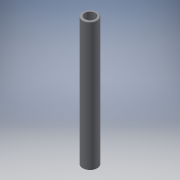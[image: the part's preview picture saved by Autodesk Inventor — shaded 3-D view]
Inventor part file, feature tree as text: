
AUTODESK INVENTOR PART (.ipt)
format: ipt  version: 2016 (Build 200138000, 138)  size: 94,720 bytes
history: native  units: mm
features: extrude x1, chamfer x1, sketch x1
ambient origin geometry x8: Origin, YZ Plane, XZ Plane, XY Plane, X Axis, Y Axis, Z Axis, Center Point
bodies: Solid1 (feature_tree)
feature tree (3):
  extrude  "Extrusion1"  Depth=500.72mm
  chamfer  "Chamfer1"  Distance=500.72mm
  sketch  "Sketch1"  dims[d0=57.2mm d1=41.9mm d2=500.72mm d3=0.0mm d4=2.0mm d5=2.0mm d6=45.0deg]
